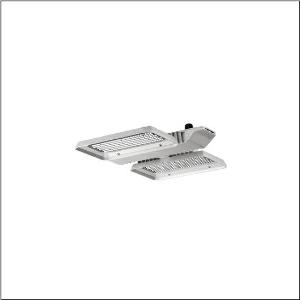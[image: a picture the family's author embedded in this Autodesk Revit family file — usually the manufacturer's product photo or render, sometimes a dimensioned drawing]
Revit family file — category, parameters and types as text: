
# Revit family: highbay_11_51hl62d14dca
name_source: partatom
category: Lighting Fixtures
units: mm (PartAtom-declared; Revit-internal decimal feet)

## family parameters
Cut with Voids When Loaded = No
Host = Face
Light Source = No
Part Type = Normal
Room Calculation Point = No
Round Connector Dimension = Use Diameter
Shared = No

## types (1)
- --- (1 x LED, 10020 lm, 55.6 W, 4000K)
    Apparent Load = 56 VA
    CIE Flux Codes = 89 96 99 100 100
    Color Rendering = 80
    Color Temperature = 4000K
    Default Elevation = 1800 mm
    Description = Highbay 11, LED high bay luminaire, primary light control with lens, of PMMA, light emission: direct distribution, primary light characteristic: symmetric, installation type: surface-mounted, suspended mounting, for 1x 2x LED, rated luminous flux: 10.020lm, luminous efficacy: 180lm/W, light colour: 840, colour temperature: 4000K, control gear: DALI, with terminal, 5-pole, max. 2.5mm², mains connection: 230..240V, AC, 50/60Hz, rated input power: 56W, LED unit, of diecast aluminium, coated, metallic grey (RAL 9006), length: 470mm, width: 500mm, height: 65mm, housing, of diecast aluminium, coated, metallic grey (RAL 9006), protection rating (complete): IP65, insulation class (complete): insulation class I (protective earthing), certification: CE, ENEC, VDE, UKCA, protection symbol: D, impact resistance: IK08 with glass or PC cover, permissible operating ambient temperature: -35..+70°C, corresponds to IFS (International Featured Standards) requirements for safety and quality in the food industry, reducing of maximum allowable ambient temperature of 5°C with ceiling mounting, packaging unit: 1 piece
    Height = 95 mm
    Lamp = 1 x LED
    Lamp Light Flux = 10020 lm
    Lamp Power = 55.6 W
    Lamp count = 1
    Length = 468 mm
    Luminous efficacy = 180 lm/W
    Manufacturer = Siteco
    ModVariant = No
    Model = 51HL62D14DCA
    Mounting Place = Ceiling
    Mounting Type = Pendant
    Number of Poles = 1
    OnlyDefault = Yes
    Power Factor = 1
    Product Name = Highbay 11
    Product group = LED high bay luminaire
    ProductGroupID = 903
    Protection Class = Protection class I
    Protection Degree = IP 65
    RLX_Detail_Level = 1
    RLX_Emergency_Light_Flux = 0 lm
    RLX_Emergency_Type = 0
    RLX_Emergency_Type_DB = No
    RlxData = <blob elided: 70377 chars, md5=801b5890>
    Socket = socket
    Standby Power = 0 W
    System Light Flux = 10020 lm
    System Power = 56 W
    Type Comments = factory setting: luminous flux: 100 % | dim-lin: 254 | 315 mA
    Type Image = l_1003425.jpg
    URL = http://relux.com
    VarID = @adj_201316
    Voltage = 0 V
    Weight = 0.00 kg
    Width = 501 mm

## geometry (parser evidence)
native form markers: Blend x4, Sweep x12
no freeform markers — native parametric forms only
